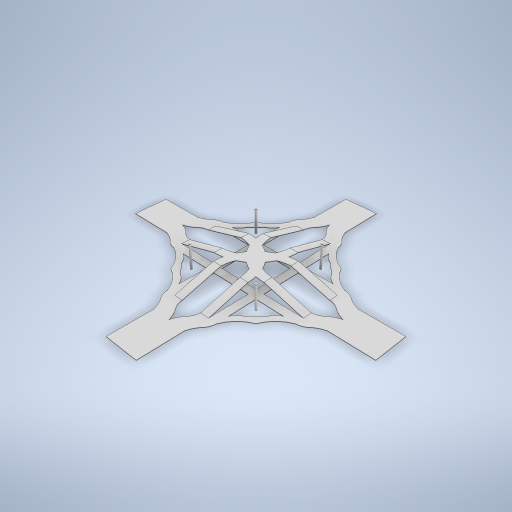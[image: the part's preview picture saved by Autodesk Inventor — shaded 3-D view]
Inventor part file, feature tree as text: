
AUTODESK INVENTOR PART (.ipt)
format: ipt  version: 2024 (Build 280153000, 153)  size: 706,560 bytes
history: native  units: in
note: dims shown in document units (in); Inventor stores cm internally (conversion verified against a paired STEP export)
features: sketch x11, plane x10, extrude x5, pattern_circular x3, mirror x2, other x2, loft x1, revolve x1
ambient origin geometry x8: Origin, YZ Plane, XZ Plane, XY Plane, X Axis, Y Axis, Z Axis, Center Point
bodies: Solid1 (feature_tree)
feature tree (35):
  extrude  "Extrusion1"  Depth=300.0in
  extrude  "Extrusion2"  TaperAngle=0.0deg  [1 undecoded]
  sketch  "Sketch7"  dims[d6=1.0994in d7=200.0in d8=200.0in d9=878.4836in]
  sketch  "Sketch8"  dims[d10=0.0in d11=0.0in]
  loft  "Loft1"
  mirror  "Mirror1"
  plane  "Work Plane2"
  mirror  "Mirror2"
  sketch  "Sketch13"  dims[d12=468.3397in d13=468.3397in d14=400.0in]
  sketch  "Sketch14"  dims[d15=200.0in d16=200.0in]
  other  "Work Axis1"
  pattern_circular  "Circular Pattern1"  Count=508  [1 undecoded]
  plane  "Work Plane9"
  plane  "Work Plane10"
  extrude  "Extrusion3"  TaperAngle=0.0deg  [1 undecoded]
  extrude  "Extrusion4"  Depth=468.3397in
  pattern_circular  "Circular Pattern2"  Count=1016  [1 undecoded]
  extrude  "Extrusion5"  Depth=200.0in
  sketch  "Sketch19"  dims[d22=360.2614in]
  revolve  "Revolution1"  [1 undecoded]
  pattern_circular  "Circular Pattern3"  [2 undecoded]
  sketch  "Sketch4"  dims[d1=400.0in d2=300.0in]
  sketch  "Sketch5"  dims[d3=0.0in d4=0.0in]
  other  "Edges1"
  plane  "Work Plane1"
  plane  "Work Plane3"
  plane  "Work Plane4"
  plane  "Work Plane5"
  plane  "Work Plane6"
  plane  "Work Plane7"
  plane  "Work Plane8"
  sketch  "Sketch15"  dims[d18=200.0in d19=400.0in]
  sketch  "Sketch16"  dims[d20=676.4723in]
  sketch  "Sketch18"  dims[d21=867.9936in]
  sketch  "Sketch20"  dims[d23=366.6875in d24=968.3397in d25=968.3397in d26=472.794in d27=968.3397in d28=170.1363in d30=1.5748in d32=360.0deg d34=1436.6794in d35=2249.746in d37=10.0in d38=0.0in d39=10.0in d40=0.0in d41=200.0in d42=0.0in d43=250.0in d44=10.0in d45=0.0in d46=90.0deg d47=0.0in d48=90.0deg d52=-642.9305in d53=0.7874in d54=90.0deg d56=90.0deg d57=260.0in d58=10.0in d59=0.0in d60=1000.0in d61=0.0in d62=1.5748in d63=360.0deg d65=50.0in d66=200.0in d67=200.0in d68=550.0in d69=0.0in d70=25.0in d71=0.0in d72=180.0deg d73=1.5748in d74=360.0deg]
note: 7 required parameter values undecoded (feature->parameter linkage not recoverable at this tier; creation-order binding heuristic only, values carry confidence <= 0.55)